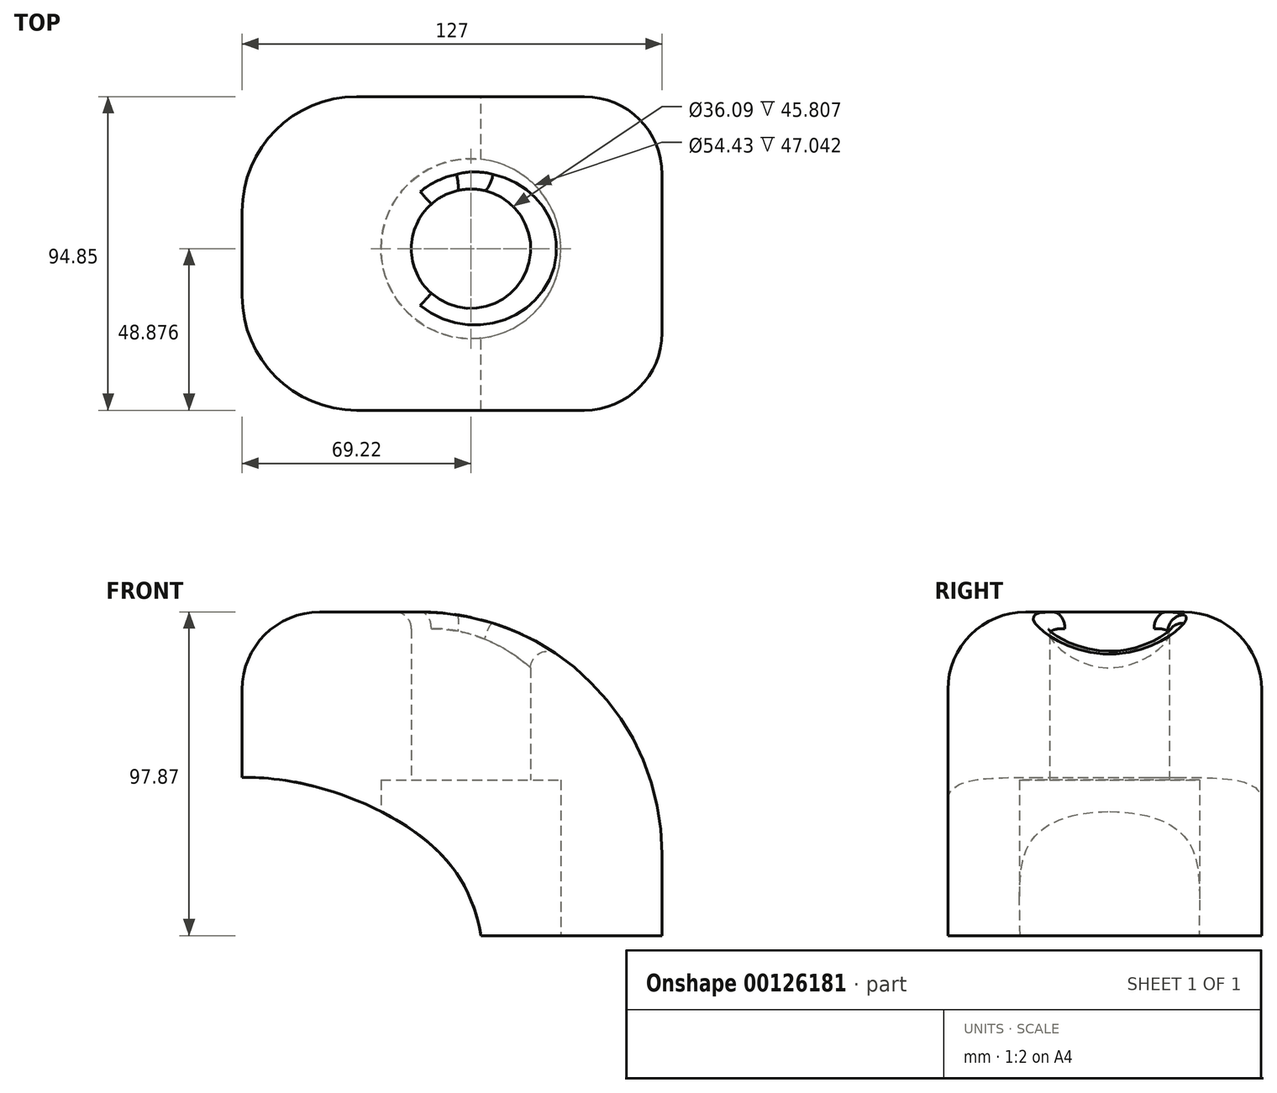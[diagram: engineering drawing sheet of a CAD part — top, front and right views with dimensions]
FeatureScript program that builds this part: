
annotation { "Feature Type Name" : "Feature", "Feature Type Description" : "" }
export const myFeature = defineFeature(function(context is Context, id is Id, definition is map)
    precondition{}
    {
        {
            var Q0;
            Q0=qCreatedBy(makeId("Front.planeOp"),FACE);
            var sketch = newSketch(context, id + "F0", { "sketchPlane" : qUnion([Q0])});
            skLineSegment(sketch, "E0.bottom", {"start": v(-62.97, 45.84) * mm, "end": v(64.03, 45.84) * mm});
            skLineSegment(sketch, "E0.top", {"start": v(-62.97, -52.03) * mm, "end": v(64.03, -52.03) * mm});
            skLineSegment(sketch, "E0.left", {"start": v(-62.97, 45.84) * mm, "end": v(-62.97, -52.03) * mm});
            skLineSegment(sketch, "E0.right", {"start": v(64.03, 45.84) * mm, "end": v(64.03, -52.03) * mm});
            skSolve(sketch);
        }
        {
            var Q0;
            Q0 = qSketchRegion(id + "F0", true);
            extrude(context, id + "F1", {"entities" : qUnion([Q0]), "depth" : 94.85 * mm});
        }
        {
            var Q0;
            Q0=makeQuery(id+"F1.opExtrude","SWEPT_EDGE",EDGE,{"disambiguationData":[OSD([sQuery(id+"F0.wireOp",EDGE,"E0.bottom"),sQuery(id+"F0.wireOp",EDGE,"E0.right")])]});
            fillet(context, id + "F2", {"entities" : qUnion([Q0]), "radius" : 73.12 * mm, "tangentPropagation" : true, "allowEdgeOverflow" : false});
        }
        {
            var Q0;
            Q0=makeQuery(id+"F1.opExtrude","CAP_EDGE",EDGE,{"disambiguationData":[OSD([sQuery(id+"F0.wireOp",EDGE,"E0.left")])],"isStart":false});
            var Q1;
            Q1=makeQuery(id+"F1.opExtrude","CAP_EDGE",EDGE,{"disambiguationData":[OSD([sQuery(id+"F0.wireOp",EDGE,"E0.left")])],"isStart":true});
            fillet(context, id + "F3", {"entities" : qUnion([Q0, Q1]), "radius" : 34.66 * mm, "tangentPropagation" : true, "allowEdgeOverflow" : false});
        }
        {
            var Q0;
            Q0=makeQuery(id+"F1.opExtrude","CAP_EDGE",EDGE,{"disambiguationData":[OSD([sQuery(id+"F0.wireOp",EDGE,"E0.right")])],"isStart":true});
            fillet(context, id + "F4", {"entities" : qUnion([Q0]), "radius" : 23.5 * mm, "tangentPropagation" : true, "allowEdgeOverflow" : false});
        }
        {
            var Q0;
            Q0=makeQuery(id+"F1.opExtrude","SWEPT_FACE",FACE,{"disambiguationData":[OSD([sQuery(id+"F0.wireOp",EDGE,"E0.top")])]});
            var sketch = newSketch(context, id + "F5", { "sketchPlane" : qUnion([Q0])});
            skCircle(sketch, "E1", {"center": v(6.25, 45.97) * mm, "radius": 18.05 * mm});
            skSolve(sketch);
        }
        {
            var Q0;
            Q0=makeQuery(id+"F5.imprint","IMPRINT",FACE,{"disambiguationData":[TD([[makeQuery(id+"F5.imprint","IMPRINT",EDGE,{"derivedFrom":sQuery(id+"F5.wireOp",EDGE,"E1")}),1.0]])]});
            extrude(context, id + "F6", {"entities" : qUnion([Q0]), "operationType" : NewBodyOperationType.REMOVE, "oppositeDirection" : true, "depth" : 164.9 * mm});
        }
        {
            var Q0;
            Q0=makeQuery(id+"F6.boolean.opBoolean","INTERSECT",EDGE,{"derivedFrom":[makeQuery(id+"F1.opExtrude","SWEPT_FACE",FACE,{"disambiguationData":[OSD([sQuery(id+"F0.wireOp",EDGE,"E0.bottom")])]}),makeQuery(id+"F6.opExtrude","SWEPT_FACE",FACE,{"disambiguationData":[OSD([sQuery(id+"F5.wireOp",EDGE,"E1")])]})]});
            fillet(context, id + "F7", {"entities" : qUnion([Q0]), "radius" : 5.02 * mm, "tangentPropagation" : true, "allowEdgeOverflow" : false});
        }
        {
            var Q0;
            Q0=makeQuery(id+"F1.opExtrude","SWEPT_FACE",FACE,{"disambiguationData":[OSD([sQuery(id+"F0.wireOp",EDGE,"E0.top")])]});
            var sketch = newSketch(context, id + "F8", { "sketchPlane" : qUnion([Q0])});
            skCircle(sketch, "E2", {"center": v(6.25, 45.97) * mm, "radius": 27.21 * mm});
            skSolve(sketch);
        }
        {
            var Q0;
            Q0 = qSketchRegion(id + "F8", true);
            extrude(context, id + "F9", {"entities" : qUnion([Q0]), "operationType" : NewBodyOperationType.REMOVE, "oppositeDirection" : true, "depth" : 47.04 * mm});
        }
        {
            var Q0;
            Q0=qCreatedBy(makeId("Front.planeOp"),FACE);
            var sketch = newSketch(context, id + "F10", { "sketchPlane" : qUnion([Q0])});
            skFitSpline(sketch, "E3", {"points": [v(-97.16, -7.95) * mm, v(-51.17, -4.9) * mm, v(0, -30.6) * mm, v(10.71, -65.44) * mm, v(10.04, -85.39) * mm], "startDerivative": vector(180.25, 18.65) * mm, "endDerivative": vector(-9.02, -100.5) * mm});
            skLineSegment(sketch, "E4", {"start": v(-97.16, -7.95) * mm, "end": v(-97.16, -83.02) * mm});
            skLineSegment(sketch, "E5", {"start": v(-97.16, -83.02) * mm, "end": v(10.04, -85.39) * mm});
            skSolve(sketch);
        }
        {
            var Q0;
            Q0=makeQuery(id+"F10.imprint","IMPRINT",FACE,{"disambiguationData":[TD([[makeQuery(id+"F10.imprint","IMPRINT",EDGE,{"derivedFrom":sQuery(id+"F10.wireOp",EDGE,"E3")}),-1.0]])]});
            extrude(context, id + "F11", {"entities" : qUnion([Q0]), "operationType" : NewBodyOperationType.REMOVE, "endBound" : BoundingType.THROUGH_ALL, "depth" : 25.4 * mm});
        }
    });
